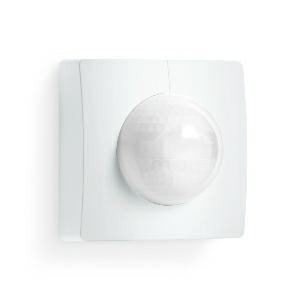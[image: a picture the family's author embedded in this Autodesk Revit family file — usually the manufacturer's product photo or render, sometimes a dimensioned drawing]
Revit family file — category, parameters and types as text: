
# Revit family: is_3180_058135
name_source: partatom
category: Elektroinstallationen
revit_build: Autodesk Revit 2016 (Build: 20190508_0715(x64)
units: mm (PartAtom-declared; Revit-internal decimal feet)

## family parameters
Basisbauteil = Fläche
Beim Laden mit Abzugskörper schneiden = Nein
Bemaßung runder Anschluss = Durchmesser verwenden
Beschriftungsausrichtung beibehalten = Nein
Gemeinsam genutzt = Nein
Raumberechnungspunkt = Nein
Teiletyp = Normal

## types (1)
- IS 3180
    Apparent Load = 0 VA
    Beschreibung = Type: Motion detectors; Dimensions (L x W x H): 65 x 95 x 95 mm; Sensor Technology: passive infrared; Application, place: Outdoors, Indoors; Application, room: corridor / aisle, function room / ancillary room, stairwell, multi-storey / underground car park, outdoors, all round the building, courtyard & driveway, Indoors; Installation site: wall, corner; Installation: Surface wiring; Mounting height: 1,80 – 2,50 m; Optimum mounting height: 2 m; Detection angle: 180 °; Sneak-by guard: Yes; Reach, radial: r = 4 m (25 m²); Reach, tangential: r = 20 m (628 m²); Twilight setting TEACH: Yes; Twilight setting: 2 – 1000 lx; Time setting: 0 sec – 1092 min; Basic light level function: Yes; KNX functions: Photo-cell controller, Basic light level function, Light level, HVAC output, Constant-lighting control, Light output 2x, Presence output, Day / night function; With bus coupling: Yes; Settings via: ETS software, Remote control, Bus, Smart Remote; IP-rating: IP54; Material: Plastic; Ambient temperature: -20 – 50 °C; Colour: white; Version: KNX - surface, sq.; PU1, EAN: 4007841058135
    Height = 95 mm
    Hersteller = Steinel
    Length = 65 mm
    Maximum range = 22.153 m
    ModVariant = Nein
    Modell = 058135
    Mounting Type = Surface mounted
    Number of Poles = 1
    OnlyDefault = Ja
    Power Factor = 1
    Product Name = IS 3180
    Product group = Sensor-switched indoor light
    ProductGroupID = 30
    Protection Class = Protection class
    Protection Degree = IP 54
    RlxData = <blob elided: 166377 chars, md5=07a60fb3>
    Sensor characteristics = Semi circular 145°-300°
    Sensor type = Passive (infrared)
    SensorDataFile = <blob elided: 5082 chars, md5=d953030a>
    Type of entry = Motion
    Typenbild = produkt1_058135.jpg
    Typenkommentare = Product without accessories
    URL = http://relux.com
    VarID = ---
    Voltage = 0 V
    Vorgabe-Ansicht = 1800 mm
    Weight = 0.00 kg
    Width = 95 mm

## geometry (parser evidence)
native form markers: Sweep x16
no freeform markers — native parametric forms only
